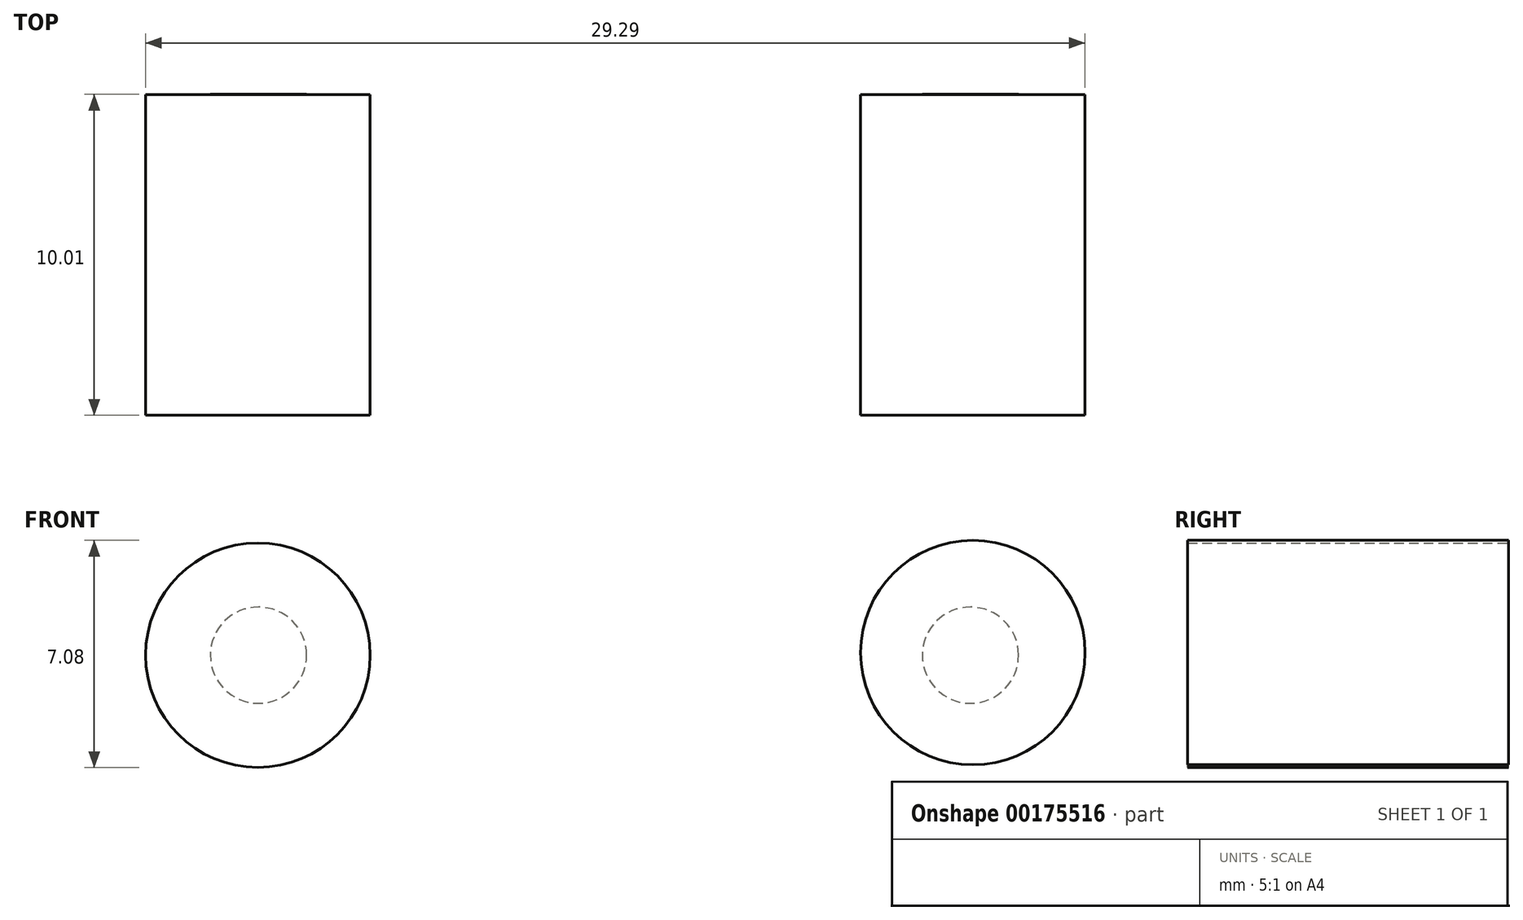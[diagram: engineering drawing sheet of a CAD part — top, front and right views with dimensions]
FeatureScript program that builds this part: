
annotation { "Feature Type Name" : "Feature", "Feature Type Description" : "" }
export const myFeature = defineFeature(function(context is Context, id is Id, definition is map)
    precondition{}
    {
        {
            var Q0;
            Q0=qCreatedBy(makeId("Front.planeOp"),FACE);
            var sketch = newSketch(context, id + "F0", { "sketchPlane" : qUnion([Q0])});
            skCircle(sketch, "E0", {"center": v(-10.98, 0) * mm, "radius": 3.5 * mm});
            skCircle(sketch, "E1", {"center": v(11.31, 0.08) * mm, "radius": 3.5 * mm});
            skSolve(sketch);
        }
        {
            var Q0;
            Q0=qSketchRegion(id+"F0",true);
            extrude(context, id + "F1", {"entities" : qUnion([Q0]), "depth" : 10 * mm});
        }
        {
            var Q0;
            Q0=qCreatedBy(makeId("Front.planeOp"),FACE);
            var sketch = newSketch(context, id + "F2", { "sketchPlane" : qUnion([Q0])});
            skCircle(sketch, "E2", {"center": v(-10.96, 0) * mm, "radius": 1.5 * mm});
            skCircle(sketch, "E3", {"center": v(11.24, 0) * mm, "radius": 1.5 * mm});
            skSolve(sketch);
        }
        {
            var Q0;
            Q0=qSketchRegion(id+"F2",true);
            extrude(context, id + "F3", {"entities" : qUnion([Q0]), "oppositeDirection" : true, "depth" : 0.01 * mm});
        }
    });
